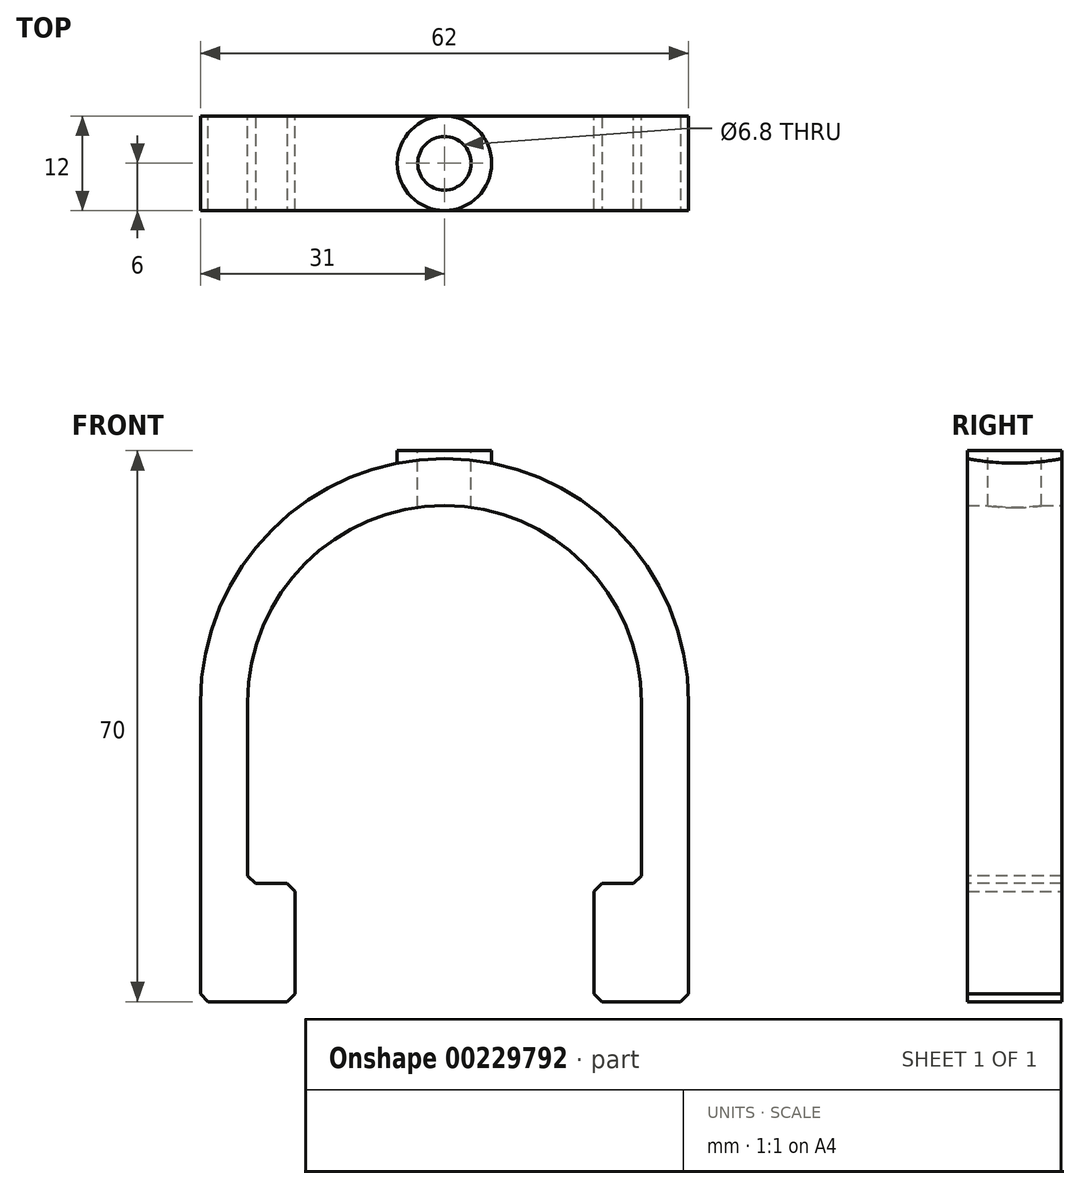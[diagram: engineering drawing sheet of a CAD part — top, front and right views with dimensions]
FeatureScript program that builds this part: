
annotation { "Feature Type Name" : "Feature", "Feature Type Description" : "" }
export const myFeature = defineFeature(function(context is Context, id is Id, definition is map)
    precondition{}
    {
        {
            var Q0;
            Q0=qCreatedBy(makeId("Front.planeOp"),FACE);
            var sketch = newSketch(context, id + "F0", { "sketchPlane" : qUnion([Q0])});
            skArc(sketch, "E0", {"start": v(25, 0) * mm, "mid": v(0, 25) * mm, "end": v(-25, 0) * mm});
            skArc(sketch, "E1.0", {"start": v(31, 0) * mm, "mid": v(0, 31) * mm, "end": v(-31, 0) * mm});
            skLineSegment(sketch, "E2", {"start": v(-25, 0) * mm, "end": v(-25, -23) * mm});
            skLineSegment(sketch, "E3", {"start": v(-25, -23) * mm, "end": v(-19, -23) * mm});
            skLineSegment(sketch, "E4", {"start": v(-19, -23) * mm, "end": v(-19, -38) * mm});
            skLineSegment(sketch, "E5", {"start": v(-19, -38) * mm, "end": v(-31, -38) * mm});
            skLineSegment(sketch, "E6", {"start": v(-31, -38) * mm, "end": v(-31, 0) * mm});
            skLineSegment(sketch, "E7.MirrorCS", {"start": v(19, -38) * mm, "end": v(31, -38) * mm});
            skLineSegment(sketch, "E8.MirrorCS", {"start": v(25, -23) * mm, "end": v(19, -23) * mm});
            skLineSegment(sketch, "E9.MirrorCS", {"start": v(19, -23) * mm, "end": v(19, -38) * mm});
            skLineSegment(sketch, "E10.MirrorCS", {"start": v(25, 0) * mm, "end": v(25, -23) * mm});
            skLineSegment(sketch, "E11.MirrorCS", {"start": v(31, -38) * mm, "end": v(31, 0) * mm});
            skSolve(sketch);
        }
        {
            var Q0;
            Q0=makeQuery(id+"F0.imprint","IMPRINT",FACE,{"disambiguationData":[TD([[makeQuery(id+"F0.imprint","IMPRINT",EDGE,{"derivedFrom":sQuery(id+"F0.wireOp",EDGE,"E0")}),-1.0]])]});
            extrude(context, id + "F1", {"entities" : qUnion([Q0]), "endBound" : BoundingType.SYMMETRIC, "depth" : 12 * mm});
        }
        {
            var Q0;
            Q0=makeQuery(id+"F1.opExtrude","SWEPT_EDGE",EDGE,{"disambiguationData":[OSD([sQuery(id+"F0.wireOp",EDGE,"E2"),sQuery(id+"F0.wireOp",EDGE,"E3")])]});
            var Q1;
            Q1=makeQuery(id+"F1.opExtrude","SWEPT_EDGE",EDGE,{"disambiguationData":[OSD([sQuery(id+"F0.wireOp",EDGE,"E3"),sQuery(id+"F0.wireOp",EDGE,"E4")])]});
            var Q2;
            Q2=makeQuery(id+"F1.opExtrude","SWEPT_EDGE",EDGE,{"disambiguationData":[OSD([sQuery(id+"F0.wireOp",EDGE,"E4"),sQuery(id+"F0.wireOp",EDGE,"E5")])]});
            var Q3;
            Q3=makeQuery(id+"F1.opExtrude","SWEPT_EDGE",EDGE,{"disambiguationData":[OSD([sQuery(id+"F0.wireOp",EDGE,"E5"),sQuery(id+"F0.wireOp",EDGE,"E6")])]});
            var Q4;
            Q4=makeQuery(id+"F1.opExtrude","SWEPT_EDGE",EDGE,{"disambiguationData":[OSD([sQuery(id+"F0.wireOp",EDGE,"E7.MirrorCS"),sQuery(id+"F0.wireOp",EDGE,"E9.MirrorCS")])]});
            var Q5;
            Q5=makeQuery(id+"F1.opExtrude","SWEPT_EDGE",EDGE,{"disambiguationData":[OSD([sQuery(id+"F0.wireOp",EDGE,"E7.MirrorCS"),sQuery(id+"F0.wireOp",EDGE,"E11.MirrorCS")])]});
            var Q6;
            Q6=makeQuery(id+"F1.opExtrude","SWEPT_EDGE",EDGE,{"disambiguationData":[OSD([sQuery(id+"F0.wireOp",EDGE,"E8.MirrorCS"),sQuery(id+"F0.wireOp",EDGE,"E10.MirrorCS")])]});
            var Q7;
            Q7=makeQuery(id+"F1.opExtrude","SWEPT_EDGE",EDGE,{"disambiguationData":[OSD([sQuery(id+"F0.wireOp",EDGE,"E8.MirrorCS"),sQuery(id+"F0.wireOp",EDGE,"E9.MirrorCS")])]});
            chamfer(context, id + "F2", {"entities" : qUnion([Q0, Q1, Q2, Q3, Q4, Q5, Q6, Q7]), "chamferType" : ChamferType.OFFSET_ANGLE, "width" : 1 * mm, "oppositeDirection" : true, "angle" : 45 * degree, "tangentPropagation" : true});
        }
        {
            var Q0;
            Q0=qCreatedBy(makeId("Top.planeOp"),FACE);
            cPlane(context, id + "F3", {"entities" : qUnion([Q0]), "cplaneType" : CPlaneType.OFFSET, "offset" : 32 * mm, "width" : 150 * mm, "height" : 150 * mm});
        }
        {
            var Q0;
            Q0=qCreatedBy(id+"F3.planeOp",FACE);
            var sketch = newSketch(context, id + "F4", { "sketchPlane" : qUnion([Q0])});
            skCircle(sketch, "E12", {"center": v(0, 0) * mm, "radius": 6 * mm});
            skSolve(sketch);
        }
        {
            var Q0;
            Q0=makeQuery(id+"F4.imprint","IMPRINT",FACE,{"disambiguationData":[TD([[makeQuery(id+"F4.imprint","IMPRINT",EDGE,{"derivedFrom":sQuery(id+"F4.wireOp",EDGE,"E12")}),1.0]])]});
            extrude(context, id + "F5", {"entities" : qUnion([Q0]), "operationType" : NewBodyOperationType.ADD, "endBound" : BoundingType.UP_TO_NEXT, "oppositeDirection" : true, "depth" : 25 * mm});
        }
        {
            var Q0;
            Q0=sQuery(id+"F4.wireOp",VERTEX,"E12.center");
            var Q1;
            Q1=makeQuery(id+"F1.opExtrude","SWEPT_BODY",BODY,{"disambiguationData":[OSD([sQuery(id+"F0.wireOp",EDGE,"E0"),sQuery(id+"F0.wireOp",EDGE,"E1.0"),sQuery(id+"F0.wireOp",EDGE,"E2"),sQuery(id+"F0.wireOp",EDGE,"E3"),sQuery(id+"F0.wireOp",EDGE,"E4"),sQuery(id+"F0.wireOp",EDGE,"E5"),sQuery(id+"F0.wireOp",EDGE,"E6"),sQuery(id+"F0.wireOp",EDGE,"E7.MirrorCS"),sQuery(id+"F0.wireOp",EDGE,"E8.MirrorCS"),sQuery(id+"F0.wireOp",EDGE,"E9.MirrorCS"),sQuery(id+"F0.wireOp",EDGE,"E10.MirrorCS"),sQuery(id+"F0.wireOp",EDGE,"E11.MirrorCS")])]});
            hole(context, id + "F6", {"style" : HoleStyle.SIMPLE, "endStyle" : HoleEndStyle.THROUGH, "standardTappedOrClearance" : lookupTablePath({ "standard" : "ISO", "engagement" : "75%", "pitch" : "1.25 mm", "size" : "M8", "type" : "Tapped" }), "standardBlindInLast" : lookupTablePath({ "standard" : "ISO", "engagement" : "75%", "pitch" : "1.25 mm", "size" : "M8", "type" : "Tapped" }), "holeDiameter" : 6.8 * mm, "startFromSketch" : true, "locations" : qUnion([Q0]), "scope" : qUnion([Q1]), "isTappedThrough" : true, "majorDiameter" : 8 * mm, "showTappedDepth" : true});
        }
    });
